# Revit family: Basin_Catch_7X20-Zurn-Z897-6
name_source: partatom
category: Plumbing Fixtures
units: mm (PartAtom-declared; Revit-internal decimal feet)

## family parameters
Always vertical = Yes
Cut with Voids When Loaded = No
Maintain Annotation Orientation = No
OmniClass Number = 23.70.50.21.24.14
OmniClass Title = Deck Waste Water Drains
Part Type = Normal
Room Calculation Point = No
Round Connector Dimension = Use Radius
Shared = No
Work Plane-Based = No

## types (8) — shared parameters
Assembly Code = D2040300
CW Connection = No
Default Elevation = 20 "
Description = 7 [178] WIDE REVEAL x 20-1/8 [511] LONGCATCH BASIN
HW Connection = No
Manufacturer = Zurn Water, LLC
Manufacurer Brand = Zurn
Modified Date = 12/08/2025
Product Documentation Link = https://files.zurn.com
Product Page URL = https://www.zurn.com
Product data url = https://www.bimobject.com
URL = www.zurn.com
Vent Connection = No
WFU = 1
Waste Connection = Yes
zero-valued in all types: CWFU, HWFU

## per-type parameters (varying)
| type | Bottom Outlet | End Outlet | Main Material | Model | Pipe Size "A" Bottom (Inner Radius) | Pipe Size "A" Bottom (Inside Diameter) | Pipe Size "A" Bottom (Nominal Diameter) | Pipe Size "A" Bottom (Nominal Radius) | Pipe Size "A" Bottom (Outer Diameter) | Pipe Size "A" Bottom (Outer Radius) | Pipe Size "A" End (Inner Diameter ) | Pipe Size "A" End (Inner Radius ) | Pipe Size "A" End (Outer Diameter) | Pipe Size "A" End(Nominal Diameter) | Pipe Size "A" End(Nominal Radius) | Pipe Size "A" End(Outer Radius) | Type Comments |
| Z897-6-E4 | No | Yes | Steel - Zurn - Stainless - Type - 304 | Z897-6 | 2.013 " | 4.026 " | 4 " | 2 " | 4.5 " | 2.25 " | 4.026 " | 2.013 " | 4.5 " | 4 " | 2 " | 2.25 " | Z897-6 with 4 Inch No-Hub End Outlet |
| Z897-6-E3 | No | Yes | Steel - Zurn - Stainless - Type - 304 | Z897-6 | 1.534 " | 3.068 " | 3 " | 1.5 " | 3.5 " | 1.75 " | 3.068 " | 1.534 " | 3.5 " | 3 " | 1.5 " | 1.75 " | Z897-6 with 3 Inch No-Hub End Outlet |
| Z897-6-U3 | Yes | No | Steel - Zurn - Stainless - Type - 304 | Z897-6 | 1.534 " | 3.068 " | 3 " | 1.5 " | 3.5 " | 1.75 " | 3.068 " | 1.534 " | 3.5 " | 3 " | 1.5 " | 1.75 " | Z897-6 with 3 Inch No-Hub Bottom Outlet |
| Z897-6-U4 | Yes | No | Steel - Zurn - Stainless - Type - 304 | Z897-6 | 2.013 " | 4.026 " | 4 " | 2 " | 4.5 " | 2.25 " | 4.026 " | 2.013 " | 4.5 " | 4 " | 2 " | 2.25 " | Z897-6 with 4 Inch No-Hub Bottom Outlet |
| ZM897-6-E4 | No | Yes | Steel - Zurn - Stainless - Type - 316 | ZN897-6 | 1.534 " | 3.068 " | 3 " | 1.5 " | 3.5 " | 1.75 " | 3.068 " | 1.534 " | 3.5 " | 3 " | 1.5 " | 1.75 " | ZM897-6 with 4 Inch No-Hub End Outlet |
| ZM897-6-E3 | No | Yes | Steel - Zurn - Stainless - Type - 316 | ZN897-6 | 1.534 " | 3.068 " | 3 " | 1.5 " | 3.5 " | 1.75 " | 3.068 " | 1.534 " | 3.5 " | 3 " | 1.5 " | 1.75 " | ZM897-6 with 3 Inch No-Hub End Outlet |
| ZM897-6-U3 | Yes | No | Steel - Zurn - Stainless - Type - 316 | ZN897-6 | 1.534 " | 3.068 " | 3 " | 1.5 " | 3.5 " | 1.75 " | 3.068 " | 1.534 " | 3.5 " | 3 " | 1.5 " | 1.75 " | ZM897-6 with 3 Inch No-Hub Bottom Outlet |
| ZM897-6-U4 | Yes | No | Steel - Zurn - Stainless - Type - 316 | ZN897-6 | 2.013 " | 4.026 " | 4 " | 2 " | 4.5 " | 2.25 " | 4.026 " | 2.013 " | 4.5 " | 4 " | 2 " | 2.25 " | ZM897-6 with 4 Inch No-Hub Bottom Outlet |

## geometry (parser evidence)
native form markers: Sweep x2
no freeform markers — native parametric forms only
